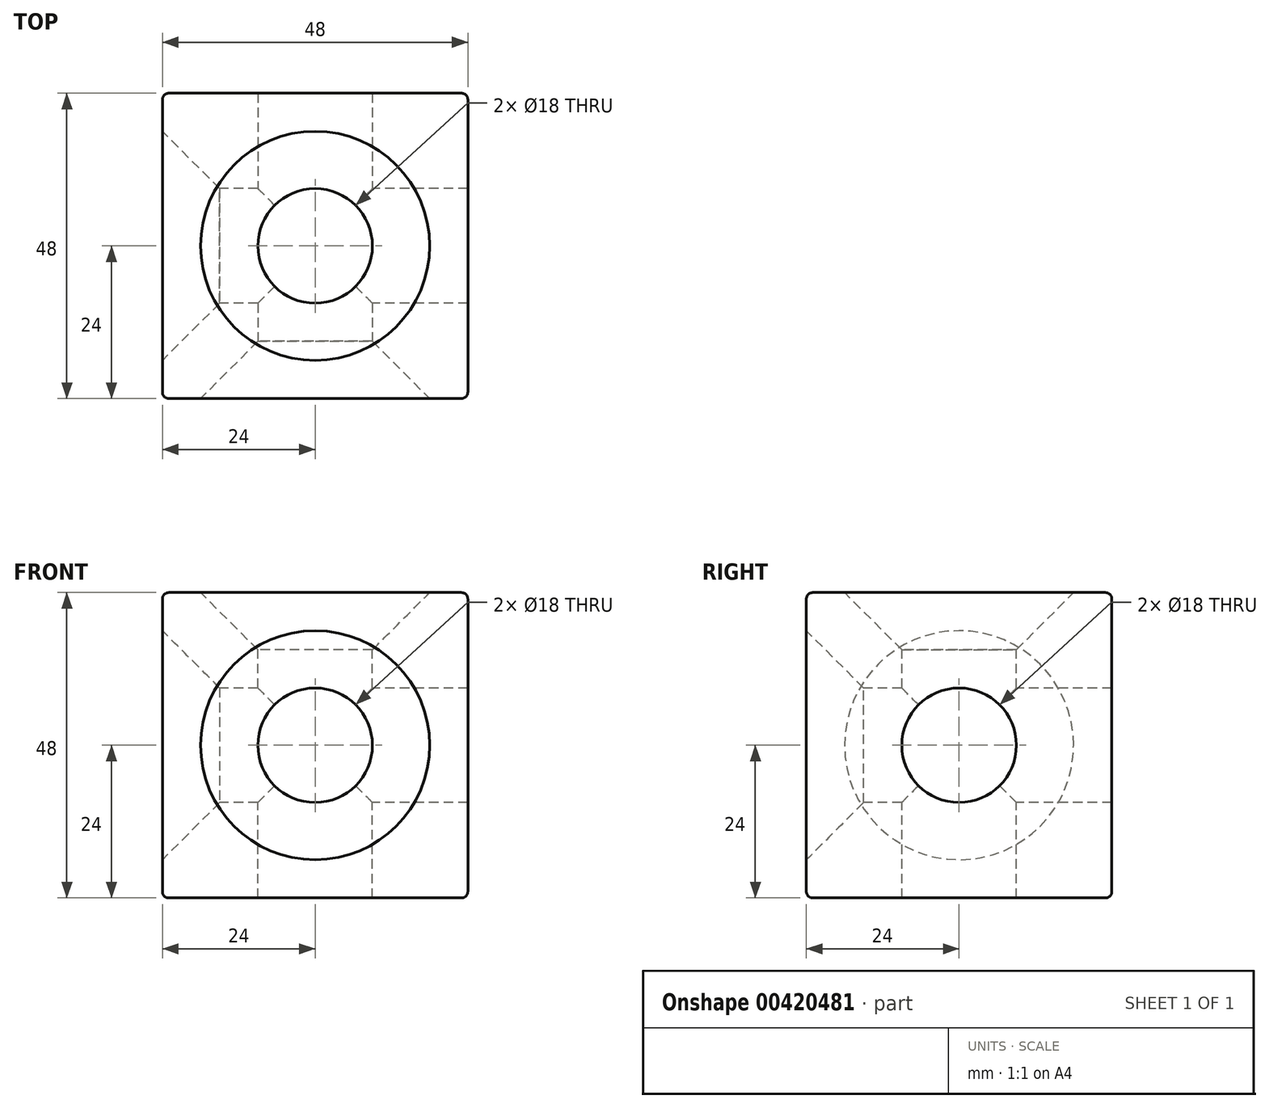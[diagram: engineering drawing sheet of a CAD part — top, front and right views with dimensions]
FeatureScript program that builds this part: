
annotation { "Feature Type Name" : "Feature", "Feature Type Description" : "" }
export const myFeature = defineFeature(function(context is Context, id is Id, definition is map)
    precondition{}
    {
        {
            var Q0;
            Q0=qCreatedBy(makeId("Front.planeOp"),FACE);
            var sketch = newSketch(context, id + "F0", { "sketchPlane" : qUnion([Q0])});
            skLineSegment(sketch, "E0.bottom", {"start": v(-24, 24) * mm, "end": v(24, 24) * mm});
            skLineSegment(sketch, "E0.top", {"start": v(-24, -24) * mm, "end": v(24, -24) * mm});
            skLineSegment(sketch, "E0.left", {"start": v(-24, 24) * mm, "end": v(-24, -24) * mm});
            skLineSegment(sketch, "E0.right", {"start": v(24, 24) * mm, "end": v(24, -24) * mm});
            skPoint(sketch, "E0.middle", {"position": v(0, 0) * mm});
            skSolve(sketch);
        }
        {
            var Q0;
            Q0=makeQuery(id+"F0.imprint","IMPRINT",FACE,{"disambiguationData":[TD([[makeQuery(id+"F0.imprint","IMPRINT",EDGE,{"derivedFrom":sQuery(id+"F0.wireOp",EDGE,"E0.bottom")}),-1.0]])]});
            extrude(context, id + "F1", {"entities" : qUnion([Q0]), "depth" : 48 * mm});
        }
        {
            var Q0;
            Q0=makeQuery(id+"F1.opExtrude","SWEPT_EDGE",EDGE,{"disambiguationData":[OSD([sQuery(id+"F0.wireOp",EDGE,"E0.bottom"),sQuery(id+"F0.wireOp",EDGE,"E0.right")])]});
            fillet(context, id + "F2", {"entities" : qUnion([Q0]), "radius" : 1 * mm, "tangentPropagation" : true, "allowEdgeOverflow" : false});
        }
        {
            var Q0;
            Q0=makeQuery(id+"F1.opExtrude","SWEPT_EDGE",EDGE,{"disambiguationData":[OSD([sQuery(id+"F0.wireOp",EDGE,"E0.bottom"),sQuery(id+"F0.wireOp",EDGE,"E0.left")])]});
            var Q1;
            Q1=makeQuery(id+"F1.opExtrude","CAP_EDGE",EDGE,{"disambiguationData":[OSD([sQuery(id+"F0.wireOp",EDGE,"E0.bottom")])],"isStart":true});
            var Q2;
            Q2=makeQuery(id+"F1.opExtrude","CAP_EDGE",EDGE,{"disambiguationData":[OSD([sQuery(id+"F0.wireOp",EDGE,"E0.bottom")])],"isStart":false});
            fillet(context, id + "F3", {"entities" : qUnion([Q0, Q1, Q2]), "radius" : 1 * mm, "tangentPropagation" : true, "allowEdgeOverflow" : false});
        }
        {
            var Q0;
            Q0=makeQuery(id+"F1.opExtrude","CAP_EDGE",EDGE,{"disambiguationData":[OSD([sQuery(id+"F0.wireOp",EDGE,"E0.left")])],"isStart":false});
            var Q1;
            {var subQ0=sQuery(id+"F0.wireOp",EDGE,"E0.right");Q1=makeQuery(id+"F3.opFillet","BLEND_EDGE",EDGE,{"blendedFrom":[makeQuery(id+"F1.opExtrude","CAP_EDGE",EDGE,{"disambiguationData":[OSD([subQ0])],"isStart":false}),makeQuery(id+"F1.opExtrude","CAP_FACE",FACE,{"disambiguationData":[OSD([sQuery(id+"F0.wireOp",EDGE,"E0.bottom"),sQuery(id+"F0.wireOp",EDGE,"E0.top"),sQuery(id+"F0.wireOp",EDGE,"E0.left"),subQ0])],"isStart":false})],"blendedInto":[makeQuery(id+"F1.opExtrude","CAP_FACE",FACE,{"disambiguationData":[OSD([sQuery(id+"F0.wireOp",EDGE,"E0.bottom"),sQuery(id+"F0.wireOp",EDGE,"E0.top"),sQuery(id+"F0.wireOp",EDGE,"E0.left"),subQ0])],"isStart":false})]});}
            var Q2;
            {var subQ0=sQuery(id+"F0.wireOp",EDGE,"E0.right");Q2=makeQuery(id+"F3.opFillet","BLEND_EDGE",EDGE,{"blendedFrom":[makeQuery(id+"F1.opExtrude","CAP_EDGE",EDGE,{"disambiguationData":[OSD([subQ0])],"isStart":true}),makeQuery(id+"F1.opExtrude","CAP_FACE",FACE,{"disambiguationData":[OSD([sQuery(id+"F0.wireOp",EDGE,"E0.bottom"),sQuery(id+"F0.wireOp",EDGE,"E0.top"),sQuery(id+"F0.wireOp",EDGE,"E0.left"),subQ0])],"isStart":true})],"blendedInto":[makeQuery(id+"F1.opExtrude","CAP_FACE",FACE,{"disambiguationData":[OSD([sQuery(id+"F0.wireOp",EDGE,"E0.bottom"),sQuery(id+"F0.wireOp",EDGE,"E0.top"),sQuery(id+"F0.wireOp",EDGE,"E0.left"),subQ0])],"isStart":true})]});}
            var Q3;
            Q3=makeQuery(id+"F1.opExtrude","CAP_EDGE",EDGE,{"disambiguationData":[OSD([sQuery(id+"F0.wireOp",EDGE,"E0.left")])],"isStart":true});
            var Q4;
            Q4=makeQuery(id+"F1.opExtrude","CAP_EDGE",EDGE,{"disambiguationData":[OSD([sQuery(id+"F0.wireOp",EDGE,"E0.top")])],"isStart":true});
            var Q5;
            Q5=makeQuery(id+"F1.opExtrude","SWEPT_EDGE",EDGE,{"disambiguationData":[OSD([sQuery(id+"F0.wireOp",EDGE,"E0.top"),sQuery(id+"F0.wireOp",EDGE,"E0.left")])]});
            var Q6;
            Q6=makeQuery(id+"F1.opExtrude","CAP_EDGE",EDGE,{"disambiguationData":[OSD([sQuery(id+"F0.wireOp",EDGE,"E0.top")])],"isStart":false});
            var Q7;
            Q7=makeQuery(id+"F1.opExtrude","SWEPT_EDGE",EDGE,{"disambiguationData":[OSD([sQuery(id+"F0.wireOp",EDGE,"E0.top"),sQuery(id+"F0.wireOp",EDGE,"E0.right")])]});
            fillet(context, id + "F4", {"entities" : qUnion([Q0, Q1, Q2, Q3, Q4, Q5, Q6, Q7]), "radius" : 1 * mm, "tangentPropagation" : true, "allowEdgeOverflow" : false});
        }
        {
            var Q0;
            Q0=makeQuery(id+"F1.opExtrude","SWEPT_FACE",FACE,{"disambiguationData":[OSD([sQuery(id+"F0.wireOp",EDGE,"E0.bottom")])]});
            var sketch = newSketch(context, id + "F5", { "sketchPlane" : qUnion([Q0])});
            skPoint(sketch, "E1", {"position": v(0, -24) * mm});
            skPoint(sketch, "E1.positionSnap0", {"position": v(23, -24) * mm});
            skSolve(sketch);
        }
        {
            var Q0;
            Q0=sQuery(id+"F5.wireOp",VERTEX,"E1");
            var Q1;
            Q1=makeQuery(id+"F1.opExtrude","SWEPT_BODY",BODY,{"disambiguationData":[OSD([sQuery(id+"F0.wireOp",EDGE,"E0.bottom"),sQuery(id+"F0.wireOp",EDGE,"E0.top"),sQuery(id+"F0.wireOp",EDGE,"E0.left"),sQuery(id+"F0.wireOp",EDGE,"E0.right")])]});
            hole(context, id + "F6", {"style" : HoleStyle.C_SINK, "endStyle" : HoleEndStyle.THROUGH, "holeDiameter" : 18 * mm, "cSinkDiameter" : 36 * mm, "cSinkAngle" : 90 * degree, "isTappedThrough" : true, "tappedDepth" : 12 * mm, "tapClearance" : 3, "locations" : qUnion([Q0]), "scope" : qUnion([Q1])});
        }
        {
            var Q0;
            Q0=makeQuery(id+"F1.opExtrude","SWEPT_FACE",FACE,{"disambiguationData":[OSD([sQuery(id+"F0.wireOp",EDGE,"E0.left")])]});
            var sketch = newSketch(context, id + "F7", { "sketchPlane" : qUnion([Q0])});
            skPoint(sketch, "E2", {"position": v(24, 0) * mm});
            skPoint(sketch, "E2.positionSnap0", {"position": v(24, 23) * mm});
            skSolve(sketch);
        }
        {
            var Q0;
            Q0=sQuery(id+"F7.wireOp",VERTEX,"E2");
            var Q1;
            Q1=makeQuery(id+"F1.opExtrude","SWEPT_BODY",BODY,{"disambiguationData":[OSD([sQuery(id+"F0.wireOp",EDGE,"E0.bottom"),sQuery(id+"F0.wireOp",EDGE,"E0.top"),sQuery(id+"F0.wireOp",EDGE,"E0.left"),sQuery(id+"F0.wireOp",EDGE,"E0.right")])]});
            hole(context, id + "F8", {"style" : HoleStyle.C_SINK, "endStyle" : HoleEndStyle.THROUGH, "holeDiameter" : 18 * mm, "cSinkDiameter" : 36 * mm, "cSinkAngle" : 90 * degree, "isTappedThrough" : true, "tappedDepth" : 12 * mm, "tapClearance" : 3, "locations" : qUnion([Q0]), "scope" : qUnion([Q1])});
        }
        {
            var Q0;
            Q0=makeQuery(id+"F1.opExtrude","CAP_FACE",FACE,{"disambiguationData":[OSD([sQuery(id+"F0.wireOp",EDGE,"E0.bottom"),sQuery(id+"F0.wireOp",EDGE,"E0.top"),sQuery(id+"F0.wireOp",EDGE,"E0.left"),sQuery(id+"F0.wireOp",EDGE,"E0.right")])],"isStart":false});
            var sketch = newSketch(context, id + "F9", { "sketchPlane" : qUnion([Q0])});
            skPoint(sketch, "E3", {"position": v(0, 0) * mm});
            skSolve(sketch);
        }
        {
            var Q0;
            Q0=sQuery(id+"F9.wireOp",VERTEX,"E3");
            var Q1;
            Q1=makeQuery(id+"F1.opExtrude","SWEPT_BODY",BODY,{"disambiguationData":[OSD([sQuery(id+"F0.wireOp",EDGE,"E0.bottom"),sQuery(id+"F0.wireOp",EDGE,"E0.top"),sQuery(id+"F0.wireOp",EDGE,"E0.left"),sQuery(id+"F0.wireOp",EDGE,"E0.right")])]});
            hole(context, id + "F10", {"style" : HoleStyle.C_SINK, "endStyle" : HoleEndStyle.THROUGH, "holeDiameter" : 18 * mm, "cSinkDiameter" : 36 * mm, "cSinkAngle" : 90 * degree, "isTappedThrough" : true, "tappedDepth" : 12 * mm, "tapClearance" : 3, "locations" : qUnion([Q0]), "scope" : qUnion([Q1])});
        }
    });
